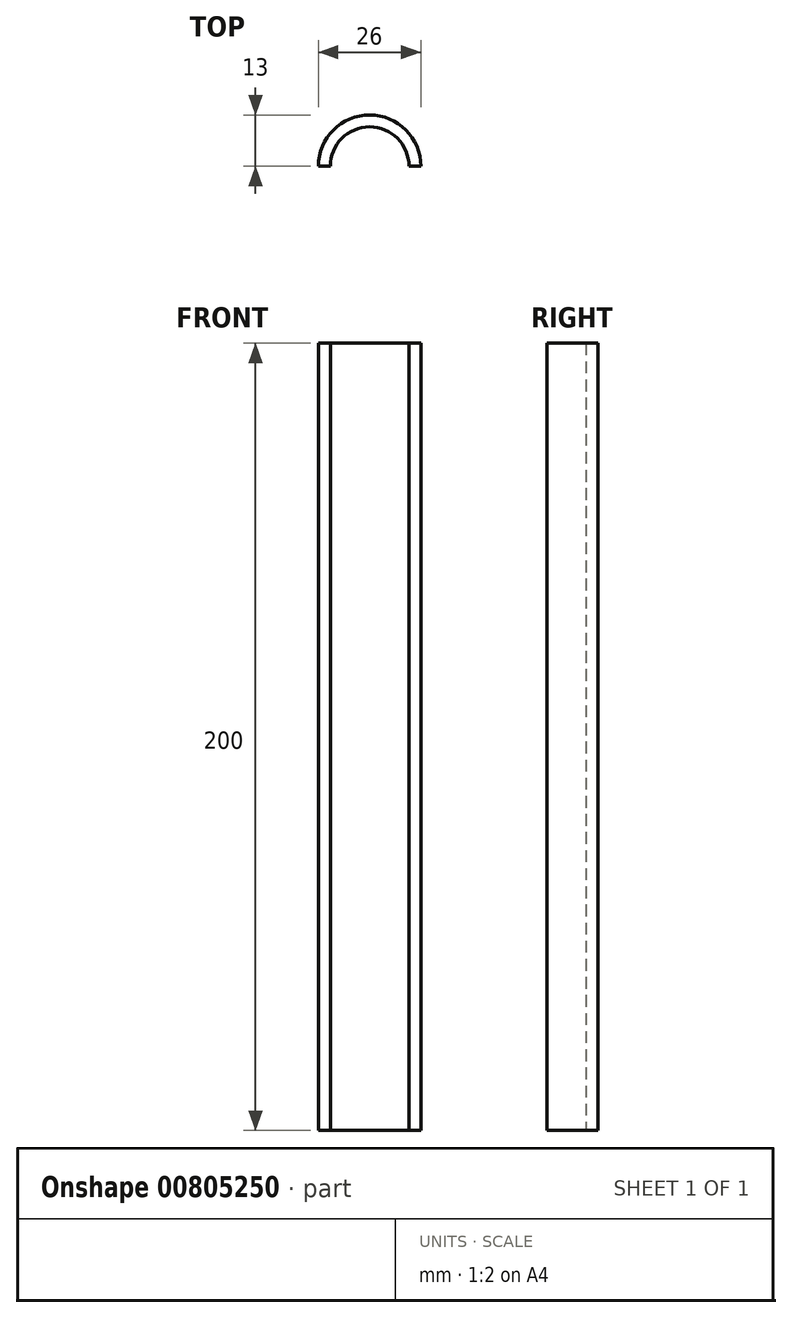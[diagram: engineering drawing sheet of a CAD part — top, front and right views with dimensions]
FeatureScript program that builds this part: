
annotation { "Feature Type Name" : "Feature", "Feature Type Description" : "" }
export const myFeature = defineFeature(function(context is Context, id is Id, definition is map)
    precondition{}
    {
        {
            var Q0;
            Q0=qCreatedBy(makeId("Top.planeOp"),FACE);
            var sketch = newSketch(context, id + "F0", { "sketchPlane" : qUnion([Q0])});
            skArc(sketch, "E0", {"start": v(-62.36, 29) * mm, "mid": v(-50.81, 34.82) * mm, "end": v(-54.65, 47.16) * mm});
            skArc(sketch, "E1.0", {"start": v(-61.66, 31.92) * mm, "mid": v(-53.58, 36) * mm, "end": v(-56.26, 44.63) * mm});
            skLineSegment(sketch, "E2", {"start": v(-63.88, 7.1) * mm, "end": v(-23.97, 7.1) * mm, "construction": true});
            skArc(sketch, "E3", {"start": v(-29.87, 7.1) * mm, "mid": v(-44.86, 22.43) * mm, "end": v(-59.86, 7.1) * mm});
            skArc(sketch, "E4", {"start": v(-39.87, -27.72) * mm, "mid": v(-49.87, -17.72) * mm, "end": v(-59.87, -27.72) * mm});
            skArc(sketch, "E5.0", {"start": v(-36.87, -27.72) * mm, "mid": v(-49.87, -14.72) * mm, "end": v(-62.87, -27.72) * mm});
            skLineSegment(sketch, "E6", {"start": v(-62.87, -27.72) * mm, "end": v(-59.87, -27.72) * mm});
            skLineSegment(sketch, "E7", {"start": v(-39.87, -27.72) * mm, "end": v(-36.87, -27.72) * mm});
            skSolve(sketch);
        }
        {
            var Q0;
            Q0 = qSketchRegion(id + "F0", true);
            extrude(context, id + "F1", {"entities" : qUnion([Q0]), "depth" : 200 * mm, "offsetDistance" : 25 * mm});
        }
    });
